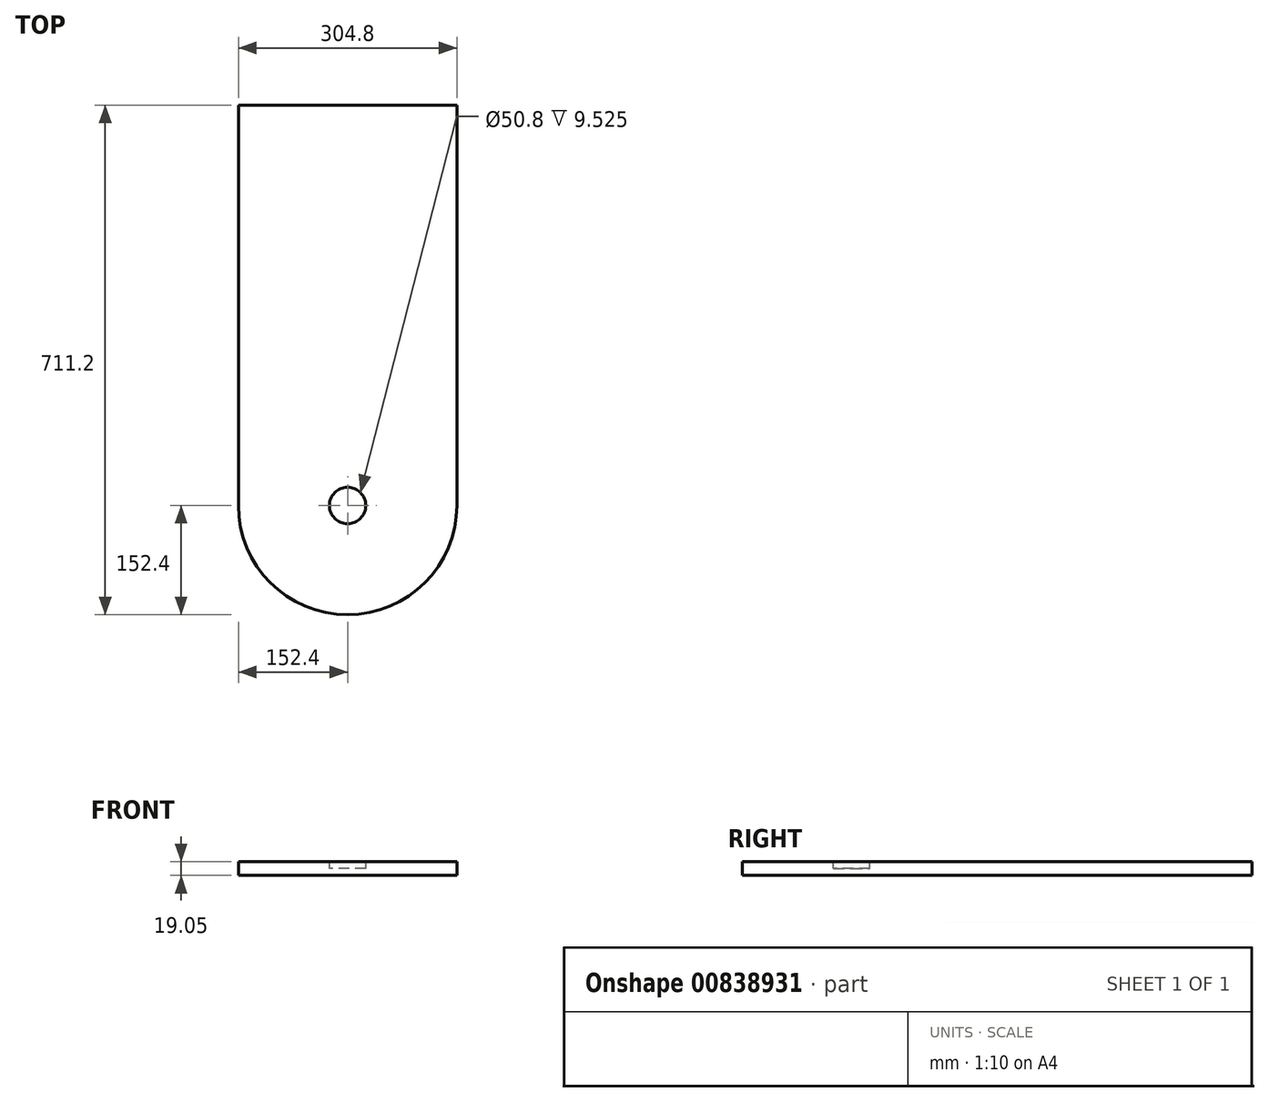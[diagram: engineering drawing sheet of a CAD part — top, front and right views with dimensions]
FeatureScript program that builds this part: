
annotation { "Feature Type Name" : "Feature", "Feature Type Description" : "" }
export const myFeature = defineFeature(function(context is Context, id is Id, definition is map)
    precondition{}
    {
        {
            var Q0;
            Q0=qCreatedBy(makeId("Top.planeOp"),FACE);
            var sketch = newSketch(context, id + "F0", { "sketchPlane" : qUnion([Q0])});
            skLineSegment(sketch, "E0", {"start": v(0, 152.4) * mm, "end": v(0, 711.2) * mm});
            skLineSegment(sketch, "E1", {"start": v(0, 711.2) * mm, "end": v(304.8, 711.2) * mm});
            skLineSegment(sketch, "E2", {"start": v(304.8, 711.2) * mm, "end": v(304.8, 152.4) * mm});
            skArc(sketch, "E3", {"start": v(0, 152.4) * mm, "mid": v(152.4, 0) * mm, "end": v(304.8, 152.4) * mm});
            skSolve(sketch);
        }
        {
            var Q0;
            Q0 = qSketchRegion(id + "F0", true);
            extrude(context, id + "F1", {"entities" : qUnion([Q0]), "depth" : 19.05 * mm, "offsetDistance" : 25.4 * mm});
        }
        {
            var Q0;
            Q0=makeQuery(id+"F1.opExtrude","CAP_FACE",FACE,{"disambiguationData":[OSD([sQuery(id+"F0.wireOp",EDGE,"E0"),sQuery(id+"F0.wireOp",EDGE,"E1"),sQuery(id+"F0.wireOp",EDGE,"E2"),sQuery(id+"F0.wireOp",EDGE,"E3")])],"isStart":false});
            var sketch = newSketch(context, id + "F2", { "sketchPlane" : qUnion([Q0])});
            skCircle(sketch, "E4", {"center": v(152.4, 152.4) * mm, "radius": 25.4 * mm});
            skSolve(sketch);
        }
        {
            var Q0;
            Q0 = qSketchRegion(id + "F2", true);
            extrude(context, id + "F3", {"entities" : qUnion([Q0]), "operationType" : NewBodyOperationType.REMOVE, "oppositeDirection" : true, "depth" : 9.52 * mm, "offsetDistance" : 25.4 * mm});
        }
    });
